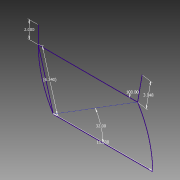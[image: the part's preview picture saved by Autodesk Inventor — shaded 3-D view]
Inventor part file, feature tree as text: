
AUTODESK INVENTOR PART (.ipt)
format: ipt  version: 2013 (Build 170138000, 138)  size: 67,072 bytes
history: native  units: in
note: dims shown in document units (in); Inventor stores cm internally (conversion verified against a paired STEP export)
features: sketch x1
ambient origin geometry x8: Origin, YZ Plane, XZ Plane, XY Plane, X Axis, Y Axis, Z Axis, Center Point
feature tree (1):
  sketch  "Sketch1"  dims[d0=11.5in d1=0.2199in d2=3.048in d3=0.6871in d4=2.0in d5=6.3397in]
